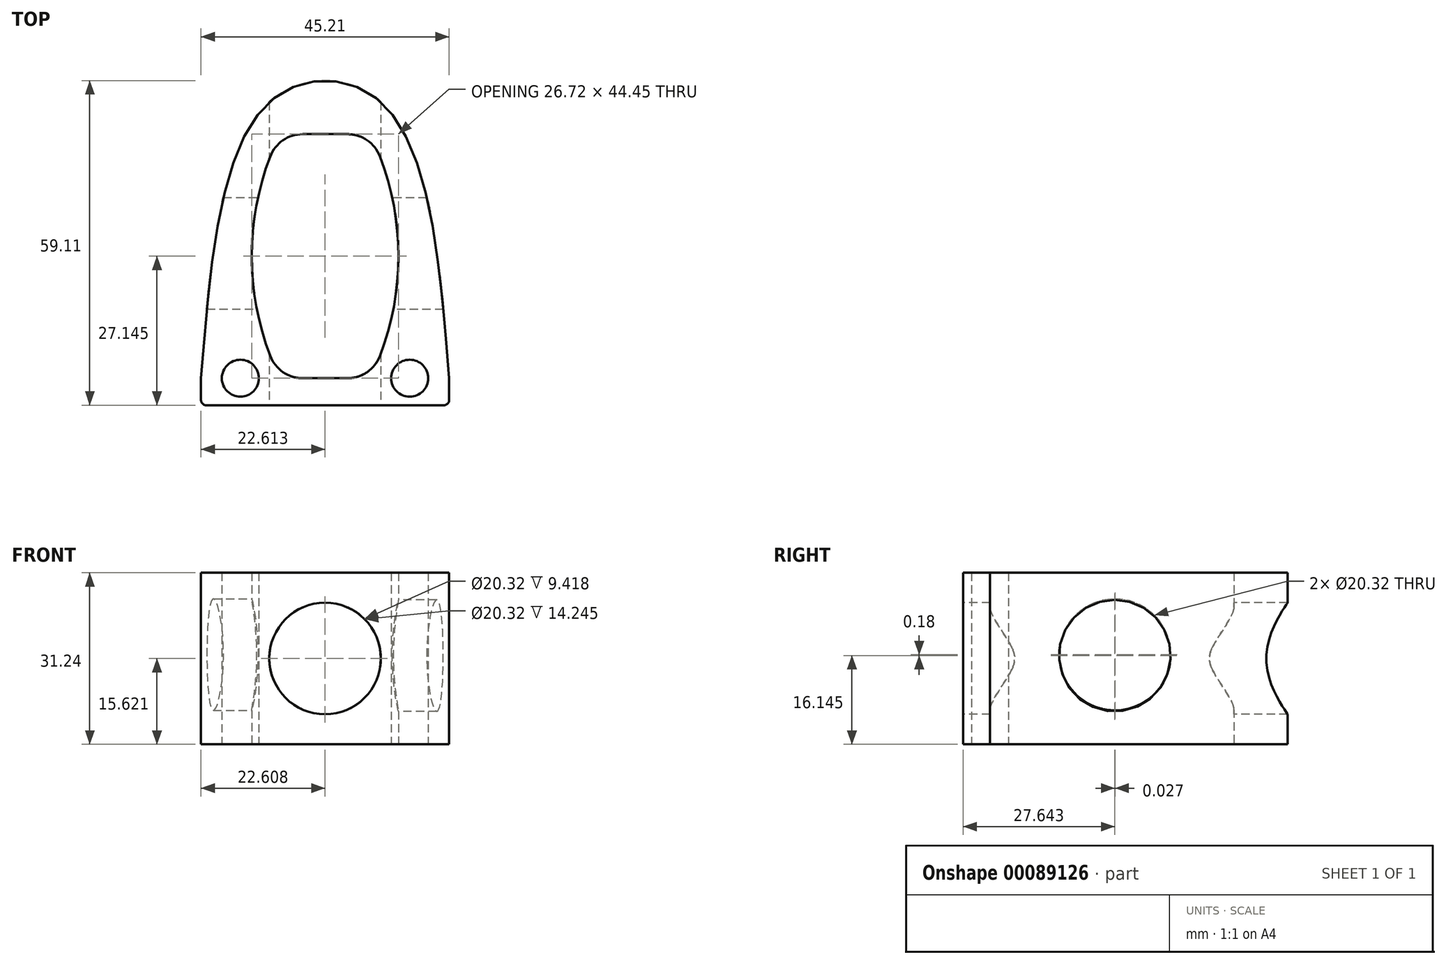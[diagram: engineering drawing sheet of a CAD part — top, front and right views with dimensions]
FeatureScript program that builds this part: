
annotation { "Feature Type Name" : "Feature", "Feature Type Description" : "" }
export const myFeature = defineFeature(function(context is Context, id is Id, definition is map)
    precondition{}
    {
        {
            var Q0;
            Q0=qCreatedBy(makeId("Top.planeOp"),FACE);
            var sketch = newSketch(context, id + "F0", { "sketchPlane" : qUnion([Q0])});
            skCircle(sketch, "E0", {"center": v(-13.35, 0) * mm, "radius": 3.37 * mm});
            skCircle(sketch, "E1", {"center": v(17.5, 0) * mm, "radius": 3.37 * mm});
            skLineSegment(sketch, "E2", {"start": v(-2, 0) * mm, "end": v(6.16, 0) * mm});
            skLineSegment(sketch, "E3", {"start": v(-20.53, 0) * mm, "end": v(-20.53, -3.95) * mm});
            skLineSegment(sketch, "E4", {"start": v(-19.56, -4.92) * mm, "end": v(23.71, -4.92) * mm});
            skLineSegment(sketch, "E5", {"start": v(24.68, -3.95) * mm, "end": v(24.68, 0) * mm});
            skArc(sketch, "E6", {"start": v(-7.93, 40.37) * mm, "mid": v(-11.28, 22.22) * mm, "end": v(-7.93, 4.08) * mm});
            skArc(sketch, "E7", {"start": v(12.1, 4.08) * mm, "mid": v(15.44, 22.22) * mm, "end": v(12.1, 40.37) * mm});
            skPoint(sketch, "E8.newPointB", {"position": v(-16.72, 0) * mm});
            skArc(sketch, "E8.filletArc", {"start": v(-7.93, 4.08) * mm, "mid": v(-5.6, 1.12) * mm, "end": v(-2, 0) * mm});
            skPoint(sketch, "E9.newPointB", {"position": v(20.87, 0) * mm});
            skArc(sketch, "E9.filletArc", {"start": v(6.16, 0) * mm, "mid": v(9.76, 1.12) * mm, "end": v(12.1, 4.08) * mm});
            skLineSegment(sketch, "E10", {"start": v(-2, 44.45) * mm, "end": v(6.16, 44.45) * mm});
            skPoint(sketch, "E11.visualSharp", {"position": v(-6.16, 44.45) * mm});
            skArc(sketch, "E11.filletArc", {"start": v(-2, 44.45) * mm, "mid": v(-5.6, 43.33) * mm, "end": v(-7.93, 40.37) * mm});
            skPoint(sketch, "E12.visualSharp", {"position": v(10.32, 44.45) * mm});
            skArc(sketch, "E12.filletArc", {"start": v(12.1, 40.37) * mm, "mid": v(9.76, 43.33) * mm, "end": v(6.16, 44.45) * mm});
            skPoint(sketch, "E13.visualSharp", {"position": v(-20.53, -4.92) * mm});
            skArc(sketch, "E13.filletArc", {"start": v(-20.53, -3.95) * mm, "mid": v(-20.24, -4.64) * mm, "end": v(-19.56, -4.92) * mm});
            skPoint(sketch, "E14.visualSharp", {"position": v(24.68, -4.92) * mm});
            skArc(sketch, "E14.filletArc", {"start": v(23.71, -4.92) * mm, "mid": v(24.4, -4.64) * mm, "end": v(24.68, -3.95) * mm});
            skFitSpline(sketch, "E15", {"points": [v(-20.53, 0) * mm, v(-7.93, 50.42) * mm, v(12.1, 50.42) * mm, v(24.68, 0) * mm], "startDerivative": vector(13.36, 166.35) * mm, "endDerivative": vector(13.33, -166.36) * mm});
            skSolve(sketch);
        }
        {
            var Q0;
            Q0=makeQuery(id+"F0.imprint","IMPRINT",FACE,{"disambiguationData":[TD([[makeQuery(id+"F0.imprint","IMPRINT",EDGE,{"derivedFrom":sQuery(id+"F0.wireOp",EDGE,"E0")}),-1.0]])]});
            extrude(context, id + "F1", {"entities" : qUnion([Q0]), "depth" : 31.24 * mm});
        }
        {
            var Q0;
            Q0=makeQuery(id+"F1.opExtrude","SWEPT_FACE",FACE,{"disambiguationData":[OSD([sQuery(id+"F0.wireOp",EDGE,"E4")])]});
            var sketch = newSketch(context, id + "F2", { "sketchPlane" : qUnion([Q0])});
            skCircle(sketch, "E16", {"center": v(2.08, 15.62) * mm, "radius": 8.9 * mm});
            skSolve(sketch);
        }
        {
            var Q0;
            Q0=sQuery(id+"F2.wireOp",VERTEX,"E16.center");
            var Q1;
            Q1=makeQuery(id+"F1.opExtrude","SWEPT_BODY",BODY,{"disambiguationData":[OSD([sQuery(id+"F0.wireOp",EDGE,"E0"),sQuery(id+"F0.wireOp",EDGE,"E1"),sQuery(id+"F0.wireOp",EDGE,"E2"),sQuery(id+"F0.wireOp",EDGE,"E3"),sQuery(id+"F0.wireOp",EDGE,"E4"),sQuery(id+"F0.wireOp",EDGE,"E5"),sQuery(id+"F0.wireOp",EDGE,"E6"),sQuery(id+"F0.wireOp",EDGE,"E7"),sQuery(id+"F0.wireOp",EDGE,"E8.filletArc"),sQuery(id+"F0.wireOp",EDGE,"E9.filletArc"),sQuery(id+"F0.wireOp",EDGE,"E10"),sQuery(id+"F0.wireOp",EDGE,"E11.filletArc"),sQuery(id+"F0.wireOp",EDGE,"E12.filletArc"),sQuery(id+"F0.wireOp",EDGE,"E13.filletArc"),sQuery(id+"F0.wireOp",EDGE,"E14.filletArc"),sQuery(id+"F0.wireOp",EDGE,"E15")])]});
            hole(context, id + "F3", {"style" : HoleStyle.SIMPLE, "endStyle" : HoleEndStyle.THROUGH, "holeDiameter" : 20.32 * mm, "locations" : qUnion([Q0]), "scope" : qUnion([Q1]), "isTappedThrough" : true});
        }
        {
            var Q0;
            Q0=qCreatedBy(makeId("Right.planeOp"),FACE);
            var sketch = newSketch(context, id + "F4", { "sketchPlane" : qUnion([Q0])});
            skCircle(sketch, "E17", {"center": v(22.72, 16.15) * mm, "radius": 9.52 * mm});
            skSolve(sketch);
        }
        {
            var Q0;
            Q0=sQuery(id+"F4.wireOp",VERTEX,"E17.center");
            var Q1;
            Q1=makeQuery(id+"F1.opExtrude","SWEPT_BODY",BODY,{"disambiguationData":[OSD([sQuery(id+"F0.wireOp",EDGE,"E0"),sQuery(id+"F0.wireOp",EDGE,"E1"),sQuery(id+"F0.wireOp",EDGE,"E2"),sQuery(id+"F0.wireOp",EDGE,"E3"),sQuery(id+"F0.wireOp",EDGE,"E4"),sQuery(id+"F0.wireOp",EDGE,"E5"),sQuery(id+"F0.wireOp",EDGE,"E6"),sQuery(id+"F0.wireOp",EDGE,"E7"),sQuery(id+"F0.wireOp",EDGE,"E8.filletArc"),sQuery(id+"F0.wireOp",EDGE,"E9.filletArc"),sQuery(id+"F0.wireOp",EDGE,"E10"),sQuery(id+"F0.wireOp",EDGE,"E11.filletArc"),sQuery(id+"F0.wireOp",EDGE,"E12.filletArc"),sQuery(id+"F0.wireOp",EDGE,"E13.filletArc"),sQuery(id+"F0.wireOp",EDGE,"E14.filletArc"),sQuery(id+"F0.wireOp",EDGE,"E15")])]});
            hole(context, id + "F5", {"style" : HoleStyle.SIMPLE, "endStyle" : HoleEndStyle.THROUGH, "oppositeDirection" : true, "holeDiameter" : 20.32 * mm, "startFromSketch" : true, "locations" : qUnion([Q0]), "scope" : qUnion([Q1]), "isTappedThrough" : true});
        }
        {
            var Q0;
            Q0=qCreatedBy(makeId("Right.planeOp"),FACE);
            var sketch = newSketch(context, id + "F6", { "sketchPlane" : qUnion([Q0])});
            skCircle(sketch, "E18", {"center": v(22.75, 16.33) * mm, "radius": 9.5 * mm});
            skSolve(sketch);
        }
        {
            var Q0;
            Q0=sQuery(id+"F6.wireOp",VERTEX,"E18.center");
            var Q1;
            Q1=makeQuery(id+"F1.opExtrude","SWEPT_BODY",BODY,{"disambiguationData":[OSD([sQuery(id+"F0.wireOp",EDGE,"E0"),sQuery(id+"F0.wireOp",EDGE,"E1"),sQuery(id+"F0.wireOp",EDGE,"E2"),sQuery(id+"F0.wireOp",EDGE,"E3"),sQuery(id+"F0.wireOp",EDGE,"E4"),sQuery(id+"F0.wireOp",EDGE,"E5"),sQuery(id+"F0.wireOp",EDGE,"E6"),sQuery(id+"F0.wireOp",EDGE,"E7"),sQuery(id+"F0.wireOp",EDGE,"E8.filletArc"),sQuery(id+"F0.wireOp",EDGE,"E9.filletArc"),sQuery(id+"F0.wireOp",EDGE,"E10"),sQuery(id+"F0.wireOp",EDGE,"E11.filletArc"),sQuery(id+"F0.wireOp",EDGE,"E12.filletArc"),sQuery(id+"F0.wireOp",EDGE,"E13.filletArc"),sQuery(id+"F0.wireOp",EDGE,"E14.filletArc"),sQuery(id+"F0.wireOp",EDGE,"E15")])]});
            hole(context, id + "F7", {"style" : HoleStyle.SIMPLE, "endStyle" : HoleEndStyle.THROUGH, "holeDiameter" : 20.32 * mm, "startFromSketch" : true, "locations" : qUnion([Q0]), "scope" : qUnion([Q1]), "isTappedThrough" : true});
        }
    });
